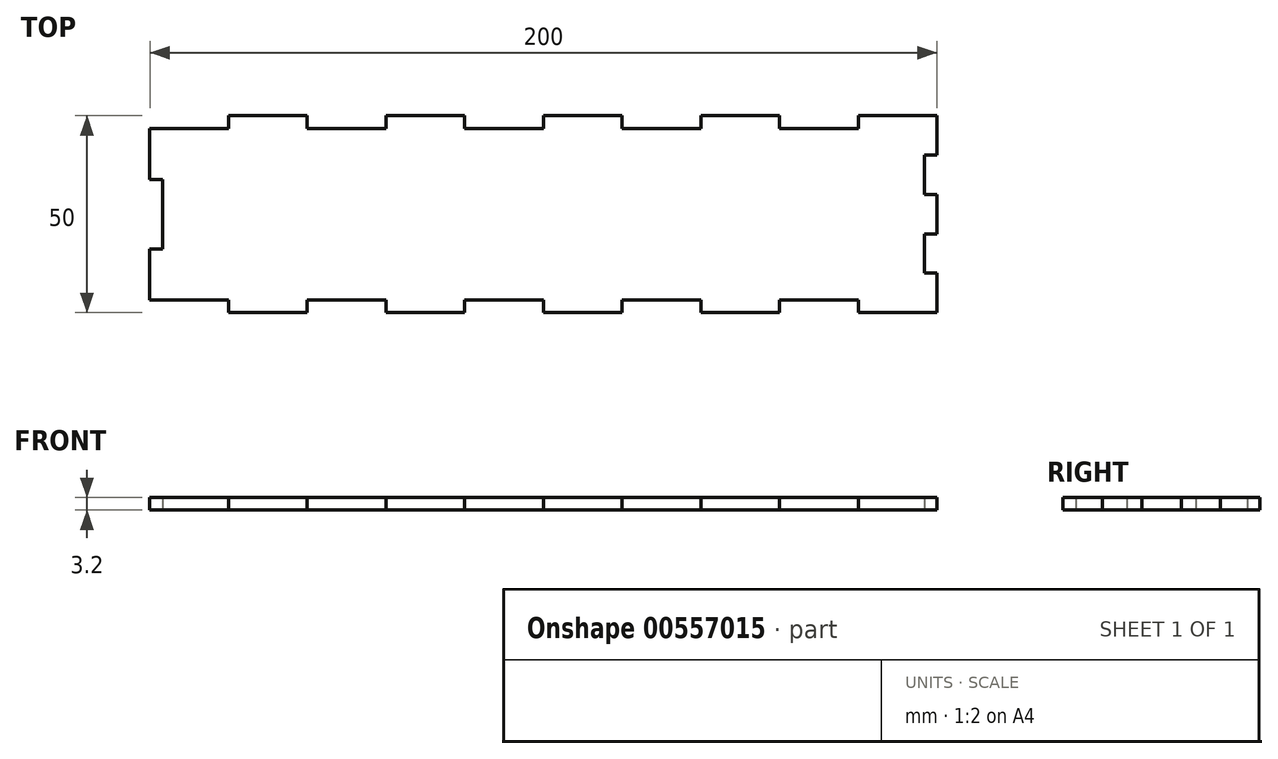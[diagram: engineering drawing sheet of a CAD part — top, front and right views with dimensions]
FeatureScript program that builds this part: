
annotation { "Feature Type Name" : "Feature", "Feature Type Description" : "" }
export const myFeature = defineFeature(function(context is Context, id is Id, definition is map)
    precondition{}
    {
        {
            var Q0;
            Q0=qCreatedBy(makeId("Top.planeOp"),FACE);
            var sketch = newSketch(context, id + "F0", { "sketchPlane" : qUnion([Q0])});
            skLineSegment(sketch, "E0.bottom", {"start": v(-85.52, 30) * mm, "end": v(-65.52, 30) * mm});
            skLineSegment(sketch, "E0.top", {"start": v(-85.52, -20) * mm, "end": v(-65.52, -20) * mm});
            skLineSegment(sketch, "E0.left", {"start": v(-105.52, 26.8) * mm, "end": v(-105.52, 13.8) * mm});
            skLineSegment(sketch, "E0.right", {"start": v(94.48, 30) * mm, "end": v(94.48, 20) * mm});
            skLineSegment(sketch, "E1.top", {"start": v(-105.52, 26.8) * mm, "end": v(-85.52, 26.8) * mm});
            skLineSegment(sketch, "E1.right", {"start": v(-85.52, 30) * mm, "end": v(-85.52, 26.8) * mm});
            skLineSegment(sketch, "E2.top", {"start": v(-65.52, 26.8) * mm, "end": v(-45.52, 26.8) * mm});
            skLineSegment(sketch, "E2.left", {"start": v(-65.52, 30) * mm, "end": v(-65.52, 26.8) * mm});
            skLineSegment(sketch, "E2.right", {"start": v(-45.52, 30) * mm, "end": v(-45.52, 26.8) * mm});
            skLineSegment(sketch, "E3.top", {"start": v(-25.52, 26.8) * mm, "end": v(-5.52, 26.8) * mm});
            skLineSegment(sketch, "E3.left", {"start": v(-25.52, 30) * mm, "end": v(-25.52, 26.8) * mm});
            skLineSegment(sketch, "E3.right", {"start": v(-5.52, 30) * mm, "end": v(-5.52, 26.8) * mm});
            skLineSegment(sketch, "E4.top", {"start": v(14.48, 26.8) * mm, "end": v(34.48, 26.8) * mm});
            skLineSegment(sketch, "E4.left", {"start": v(14.48, 30) * mm, "end": v(14.48, 26.8) * mm});
            skLineSegment(sketch, "E4.right", {"start": v(34.48, 30) * mm, "end": v(34.48, 26.8) * mm});
            skLineSegment(sketch, "E5.top", {"start": v(54.48, 26.8) * mm, "end": v(74.48, 26.8) * mm});
            skLineSegment(sketch, "E5.left", {"start": v(54.48, 30) * mm, "end": v(54.48, 26.8) * mm});
            skLineSegment(sketch, "E5.right", {"start": v(74.48, 30) * mm, "end": v(74.48, 26.8) * mm});
            skLineSegment(sketch, "E6.bottom", {"start": v(-105.52, -16.8) * mm, "end": v(-85.52, -16.8) * mm});
            skLineSegment(sketch, "E6.right", {"start": v(-85.52, -16.8) * mm, "end": v(-85.52, -20) * mm});
            skLineSegment(sketch, "E7.bottom", {"start": v(-65.52, -16.8) * mm, "end": v(-45.52, -16.8) * mm});
            skLineSegment(sketch, "E7.left", {"start": v(-65.52, -16.8) * mm, "end": v(-65.52, -20) * mm});
            skLineSegment(sketch, "E7.right", {"start": v(-45.52, -16.8) * mm, "end": v(-45.52, -20) * mm});
            skLineSegment(sketch, "E8.bottom", {"start": v(-25.52, -16.8) * mm, "end": v(-5.52, -16.8) * mm});
            skLineSegment(sketch, "E8.left", {"start": v(-25.52, -16.8) * mm, "end": v(-25.52, -20) * mm});
            skLineSegment(sketch, "E8.right", {"start": v(-5.52, -16.8) * mm, "end": v(-5.52, -20) * mm});
            skLineSegment(sketch, "E9.bottom", {"start": v(14.48, -16.8) * mm, "end": v(34.48, -16.8) * mm});
            skLineSegment(sketch, "E9.left", {"start": v(14.48, -16.8) * mm, "end": v(14.48, -20) * mm});
            skLineSegment(sketch, "E9.right", {"start": v(34.48, -16.8) * mm, "end": v(34.48, -20) * mm});
            skLineSegment(sketch, "E10.bottom", {"start": v(54.48, -16.8) * mm, "end": v(74.48, -16.8) * mm});
            skLineSegment(sketch, "E10.left", {"start": v(54.48, -16.8) * mm, "end": v(54.48, -20) * mm});
            skLineSegment(sketch, "E10.right", {"start": v(74.48, -16.8) * mm, "end": v(74.48, -20) * mm});
            skLineSegment(sketch, "E11.bottom", {"start": v(-105.52, 13.8) * mm, "end": v(-102.32, 13.8) * mm});
            skLineSegment(sketch, "E11.top", {"start": v(-105.52, -3.8) * mm, "end": v(-102.32, -3.8) * mm});
            skLineSegment(sketch, "E11.right", {"start": v(-102.32, 13.8) * mm, "end": v(-102.32, -3.8) * mm});
            skLineSegment(sketch, "E12.bottom", {"start": v(91.28, 20) * mm, "end": v(94.48, 20) * mm});
            skLineSegment(sketch, "E12.top", {"start": v(91.28, 10) * mm, "end": v(94.48, 10) * mm});
            skLineSegment(sketch, "E12.left", {"start": v(91.28, 20) * mm, "end": v(91.28, 10) * mm});
            skLineSegment(sketch, "E13.bottom", {"start": v(91.28, 0) * mm, "end": v(94.48, 0) * mm});
            skLineSegment(sketch, "E13.top", {"start": v(91.28, -10) * mm, "end": v(94.48, -10) * mm});
            skLineSegment(sketch, "E13.left", {"start": v(91.28, 0) * mm, "end": v(91.28, -10) * mm});
            skLineSegment(sketch, "E14.trimOffspring", {"start": v(74.48, 30) * mm, "end": v(94.48, 30) * mm});
            skLineSegment(sketch, "E15.trimOffspring", {"start": v(94.48, 10) * mm, "end": v(94.48, 0) * mm});
            skLineSegment(sketch, "E16.trimOffspring", {"start": v(94.48, -10) * mm, "end": v(94.48, -20) * mm});
            skLineSegment(sketch, "E17.trimOffspring", {"start": v(74.48, -20) * mm, "end": v(94.48, -20) * mm});
            skLineSegment(sketch, "E18.trimOffspring", {"start": v(34.48, -20) * mm, "end": v(54.48, -20) * mm});
            skLineSegment(sketch, "E19.trimOffspring", {"start": v(34.48, 30) * mm, "end": v(54.48, 30) * mm});
            skLineSegment(sketch, "E20.trimOffspring", {"start": v(-5.52, 30) * mm, "end": v(14.48, 30) * mm});
            skLineSegment(sketch, "E21.trimOffspring", {"start": v(-5.52, -20) * mm, "end": v(14.48, -20) * mm});
            skLineSegment(sketch, "E22.trimOffspring", {"start": v(-45.52, -20) * mm, "end": v(-25.52, -20) * mm});
            skLineSegment(sketch, "E23.trimOffspring", {"start": v(-45.52, 30) * mm, "end": v(-25.52, 30) * mm});
            skPoint(sketch, "E24.orphan", {"position": v(-105.52, 30) * mm});
            skLineSegment(sketch, "E25.trimOffspring", {"start": v(-105.52, -3.8) * mm, "end": v(-105.52, -16.8) * mm});
            skPoint(sketch, "E26.orphan", {"position": v(-105.52, -20) * mm});
            skSolve(sketch);
        }
        {
            var Q0;
            Q0=qSketchRegion(id+"F0",true);
            extrude(context, id + "F1", {"entities" : qUnion([Q0]), "depth" : 3.2 * mm});
        }
    });
